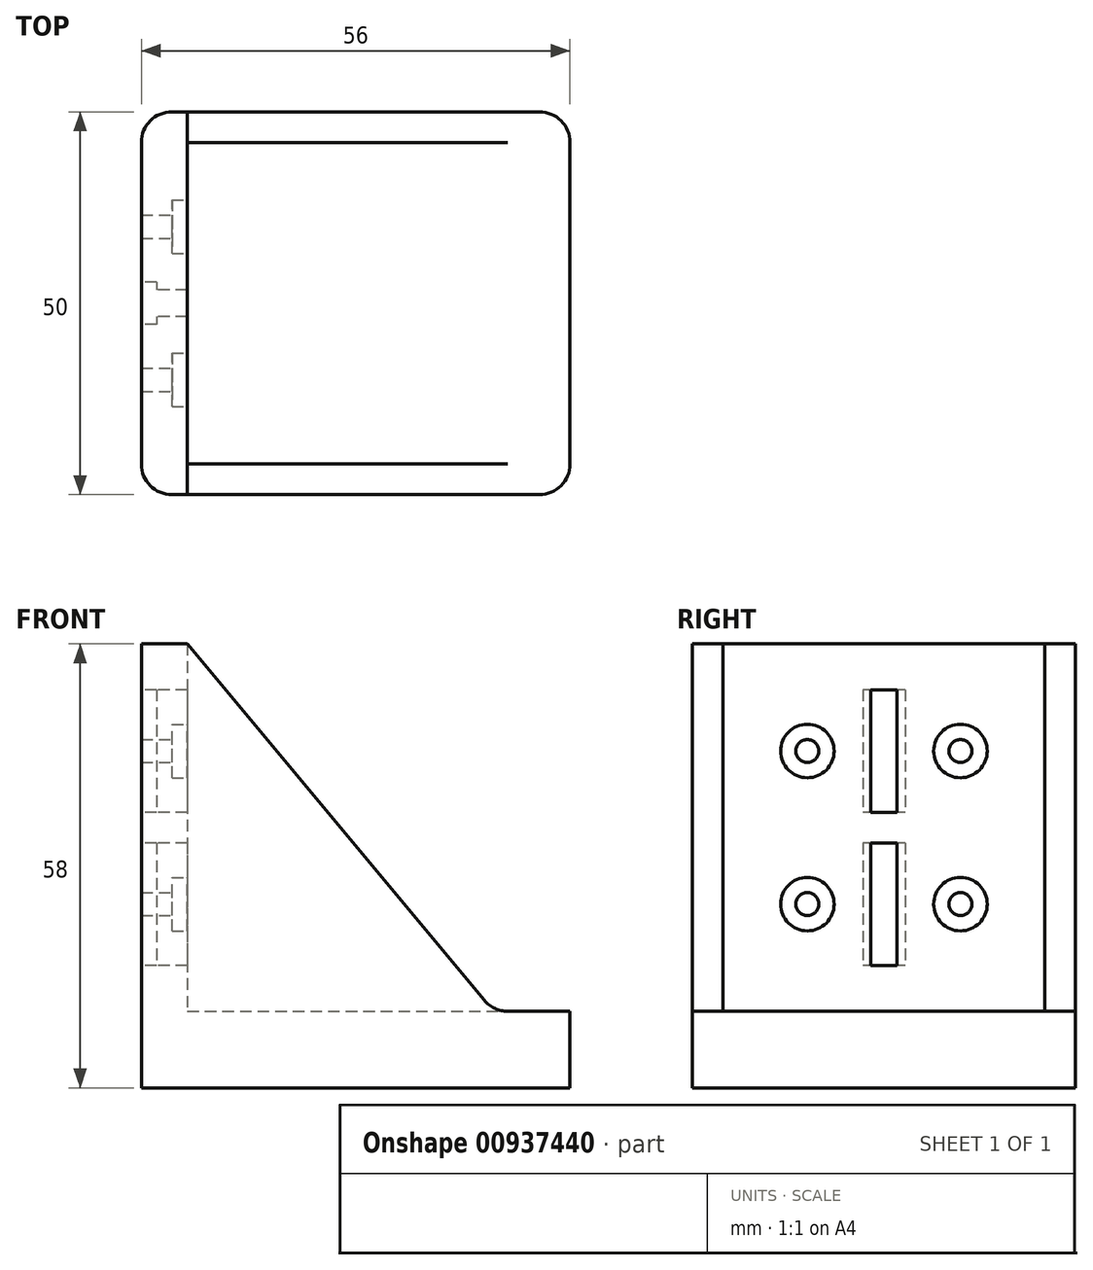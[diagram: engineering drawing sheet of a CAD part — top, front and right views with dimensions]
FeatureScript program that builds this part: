
annotation { "Feature Type Name" : "Feature", "Feature Type Description" : "" }
export const myFeature = defineFeature(function(context is Context, id is Id, definition is map)
    precondition{}
    {
        {
            var Q0;
            Q0=qCreatedBy(makeId("Top.planeOp"),FACE);
            var sketch = newSketch(context, id + "F0", { "sketchPlane" : qUnion([Q0])});
            skLineSegment(sketch, "E0.bottom", {"start": v(0, 50) * mm, "end": v(56, 50) * mm});
            skLineSegment(sketch, "E0.top", {"start": v(0, 0) * mm, "end": v(56, 0) * mm});
            skLineSegment(sketch, "E0.left", {"start": v(0, 50) * mm, "end": v(0, 0) * mm});
            skLineSegment(sketch, "E0.right", {"start": v(56, 50) * mm, "end": v(56, 0) * mm});
            skSolve(sketch);
        }
        {
            var Q0;
            Q0=qSketchRegion(id+"F0",true);
            extrude(context, id + "F1", {"entities" : qUnion([Q0]), "depth" : 10 * mm, "offsetDistance" : 25 * mm});
        }
        {
            var Q0;
            Q0=makeQuery(id+"F1.opExtrude","CAP_FACE",FACE,{"disambiguationData":[OSD([sQuery(id+"F0.wireOp",EDGE,"JcqLtr4a-4iO0-7SYc-JrXt-3wWf4lI9VCyy"),sQuery(id+"F0.wireOp",EDGE,"3zeIyssa-BI9L-WOF6-APSg-kyZtDzQDufFM"),sQuery(id+"F0.wireOp",EDGE,"Hb38dC7V-6ZDo-NrQG-Z8Se-XjxkW8JbUmMz"),sQuery(id+"F0.wireOp",EDGE,"y3aIqdCw-jFc2-MhhD-7X5v-KuRHTVy27k4Q"),sQuery(id+"F0.wireOp",EDGE,"XVNT8TL3-6rPS-E8CT-cUIb-nR5d3DAh4WGq"),sQuery(id+"F0.wireOp",EDGE,"E0.bottom"),sQuery(id+"F0.wireOp",EDGE,"E0.top"),sQuery(id+"F0.wireOp",EDGE,"E0.left"),sQuery(id+"F0.wireOp",EDGE,"E0.right")])],"isStart":false});
            var sketch = newSketch(context, id + "F2", { "sketchPlane" : qUnion([Q0])});
            skLineSegment(sketch, "E1.bottom", {"start": v(0, 50) * mm, "end": v(6, 50) * mm});
            skLineSegment(sketch, "E1.top", {"start": v(0, 0) * mm, "end": v(6, 0) * mm});
            skLineSegment(sketch, "E1.left", {"start": v(0, 50) * mm, "end": v(0, 0) * mm});
            skLineSegment(sketch, "E1.right", {"start": v(6, 50) * mm, "end": v(6, 0) * mm});
            skLineSegment(sketch, "E2.bottom", {"start": v(6, 50) * mm, "end": v(46, 50) * mm});
            skLineSegment(sketch, "E2.top", {"start": v(6, 46) * mm, "end": v(46, 46) * mm});
            skLineSegment(sketch, "E2.left", {"start": v(6, 50) * mm, "end": v(6, 46) * mm});
            skLineSegment(sketch, "E2.right", {"start": v(46, 50) * mm, "end": v(46, 46) * mm});
            skLineSegment(sketch, "E3.bottom", {"start": v(6, 0) * mm, "end": v(46, 0) * mm});
            skLineSegment(sketch, "E3.top", {"start": v(6, 4) * mm, "end": v(46, 4) * mm});
            skLineSegment(sketch, "E3.left", {"start": v(6, 0) * mm, "end": v(6, 4) * mm});
            skLineSegment(sketch, "E3.right", {"start": v(46, 0) * mm, "end": v(46, 4) * mm});
            skSolve(sketch);
        }
        {
            var Q0;
            Q0=qSketchRegion(id+"F2",true);
            extrude(context, id + "F3", {"entities" : qUnion([Q0]), "operationType" : NewBodyOperationType.ADD, "depth" : (25 + 15 + 8) * mm, "offsetDistance" : 25 * mm});
        }
        {
            var Q0;
            Q0=makeQuery(id+"F3.boolean.opBoolean","MERGE",FACE,{"derivedFrom":[makeQuery(id+"F1.opExtrude","SWEPT_FACE",FACE,{"disambiguationData":[OSD([sQuery(id+"F0.wireOp",EDGE,"E0.top")])]}),makeQuery(id+"F3.opExtrude","SWEPT_FACE",FACE,{"disambiguationData":[OSD([sQuery(id+"F2.wireOp",EDGE,"E1.top"),sQuery(id+"F2.wireOp",EDGE,"E3.bottom")])]})]});
            var sketch = newSketch(context, id + "F4", { "sketchPlane" : qUnion([Q0])});
            skLineSegment(sketch, "E4", {"start": v(46, 10) * mm, "end": v(6, 58) * mm});
            skLineSegment(sketch, "E5", {"start": v(6, 58) * mm, "end": v(46, 58) * mm});
            skLineSegment(sketch, "E6", {"start": v(46, 58) * mm, "end": v(46, 10) * mm});
            skSolve(sketch);
        }
        {
            var Q0;
            Q0 = qSketchRegion(id + "F4", true);
            extrude(context, id + "F5", {"entities" : qUnion([Q0]), "operationType" : NewBodyOperationType.REMOVE, "endBound" : BoundingType.THROUGH_ALL, "oppositeDirection" : true, "depth" : 25 * mm, "offsetDistance" : 25 * mm});
        }
        {
            var Q0;
            Q0=makeQuery(id+"F3.boolean.opBoolean","MERGE",EDGE,{"derivedFrom":[makeQuery(id+"F1.opExtrude","SWEPT_EDGE",EDGE,{"disambiguationData":[OSD([sQuery(id+"F0.wireOp",EDGE,"E0.top"),sQuery(id+"F0.wireOp",EDGE,"E0.left")])]}),makeQuery(id+"F3.opExtrude","SWEPT_EDGE",EDGE,{"disambiguationData":[OSD([sQuery(id+"F2.wireOp",EDGE,"E1.top"),sQuery(id+"F2.wireOp",EDGE,"E1.left")])]})]});
            var Q1;
            Q1=makeQuery(id+"F1.opExtrude","SWEPT_EDGE",EDGE,{"disambiguationData":[OSD([sQuery(id+"F0.wireOp",EDGE,"E0.top"),sQuery(id+"F0.wireOp",EDGE,"E0.right")])]});
            var Q2;
            Q2=makeQuery(id+"F5.boolean.opBoolean","MERGE",EDGE,{"derivedFrom":[makeQuery(id+"F3.opExtrude","CAP_EDGE",EDGE,{"disambiguationData":[OSD([sQuery(id+"F2.wireOp",EDGE,"E3.right")])],"isStart":true})],"fromTools":[makeQuery(id+"F5.opExtrude","SWEPT_EDGE",EDGE,{"disambiguationData":[OSD([sQuery(id+"F0.wireOp",EDGE,"E0.top"),sQuery(id+"F4.wireOp",EDGE,"E4"),sQuery(id+"F4.wireOp",EDGE,"E6")])]})]});
            var Q3;
            Q3=makeQuery(id+"F5.boolean.opBoolean","MERGE",EDGE,{"derivedFrom":[makeQuery(id+"F3.opExtrude","CAP_EDGE",EDGE,{"disambiguationData":[OSD([sQuery(id+"F2.wireOp",EDGE,"E2.right")])],"isStart":true})],"fromTools":[makeQuery(id+"F5.opExtrude","SWEPT_EDGE",EDGE,{"disambiguationData":[OSD([sQuery(id+"F0.wireOp",EDGE,"E0.top"),sQuery(id+"F4.wireOp",EDGE,"E4"),sQuery(id+"F4.wireOp",EDGE,"E6")])]})]});
            var Q4;
            Q4=makeQuery(id+"F1.opExtrude","SWEPT_EDGE",EDGE,{"disambiguationData":[OSD([sQuery(id+"F0.wireOp",EDGE,"E0.bottom"),sQuery(id+"F0.wireOp",EDGE,"E0.right")])]});
            var Q5;
            Q5=makeQuery(id+"F3.boolean.opBoolean","MERGE",EDGE,{"derivedFrom":[makeQuery(id+"F1.opExtrude","SWEPT_EDGE",EDGE,{"disambiguationData":[OSD([sQuery(id+"F0.wireOp",EDGE,"E0.bottom"),sQuery(id+"F0.wireOp",EDGE,"E0.left")])]}),makeQuery(id+"F3.opExtrude","SWEPT_EDGE",EDGE,{"disambiguationData":[OSD([sQuery(id+"F2.wireOp",EDGE,"E1.bottom"),sQuery(id+"F2.wireOp",EDGE,"E1.left")])]})]});
            fillet(context, id + "F6", {"entities" : qUnion([Q0, Q1, Q2, Q3, Q4, Q5]), "radius" : 4 * mm, "tangentPropagation" : true, "allowEdgeOverflow" : false});
        }
        {
            var Q0;
            Q0=makeQuery(id+"F3.boolean.opBoolean","MERGE",FACE,{"derivedFrom":[makeQuery(id+"F1.opExtrude","SWEPT_FACE",FACE,{"disambiguationData":[OSD([sQuery(id+"F0.wireOp",EDGE,"E0.left")])]}),makeQuery(id+"F3.opExtrude","SWEPT_FACE",FACE,{"disambiguationData":[OSD([sQuery(id+"F2.wireOp",EDGE,"E1.left")])]})]});
            var sketch = newSketch(context, id + "F7", { "sketchPlane" : qUnion([Q0])});
            skLineSegment(sketch, "E7", {"start": v(-25, 52) * mm, "end": v(-25, 16) * mm, "construction": true});
            skLineSegment(sketch, "E8", {"start": v(-26.73, 52) * mm, "end": v(-26.73, 16) * mm});
            skLineSegment(sketch, "E9", {"start": v(-23.28, 52) * mm, "end": v(-23.28, 16) * mm});
            skLineSegment(sketch, "E10.bottom", {"start": v(-27.76, 36) * mm, "end": v(-22.24, 36) * mm});
            skLineSegment(sketch, "E10.top", {"start": v(-27.76, 32) * mm, "end": v(-22.24, 32) * mm});
            skLineSegment(sketch, "E10.left", {"start": v(-27.76, 36) * mm, "end": v(-27.76, 32) * mm});
            skLineSegment(sketch, "E10.right", {"start": v(-22.24, 36) * mm, "end": v(-22.24, 32) * mm});
            skLineSegment(sketch, "E11", {"start": v(-25, 34) * mm, "end": v(-27.76, 34) * mm, "construction": true});
            skLineSegment(sketch, "E12", {"start": v(-23.28, 52) * mm, "end": v(-26.73, 52) * mm});
            skLineSegment(sketch, "E13", {"start": v(-23.28, 16) * mm, "end": v(-26.73, 16) * mm});
            skLineSegment(sketch, "E14.bottom", {"start": v(-27.76, 52) * mm, "end": v(-22.24, 52) * mm});
            skLineSegment(sketch, "E14.top", {"start": v(-27.76, 16) * mm, "end": v(-22.24, 16) * mm});
            skLineSegment(sketch, "E14.left", {"start": v(-27.76, 52) * mm, "end": v(-27.76, 16) * mm});
            skLineSegment(sketch, "E14.right", {"start": v(-22.24, 52) * mm, "end": v(-22.24, 16) * mm});
            skLineSegment(sketch, "E15", {"start": v(-27.76, 34) * mm, "end": v(-27.76, 34) * mm});
            skLineSegment(sketch, "E16", {"start": v(-25, 58) * mm, "end": v(-25, 52) * mm, "construction": true});
            skSolve(sketch);
        }
        {
            var Q0;
            {var subQ0=sQuery(id+"F7.wireOp",EDGE,"E14.bottom");var subQ1=sQuery(id+"F7.wireOp",EDGE,"E8");var subQ2=makeQuery(id+"F7.imprint","INTERSECT",VERTEX,{"derivedFrom":[subQ1,subQ0]});Q0=makeQuery(id+"F7.imprint","IMPRINT",FACE,{"disambiguationData":[TD([[makeQuery(id+"F7.imprint","IMPRINT",EDGE,{"disambiguationData":[TD([[subQ2,-1.0]])],"derivedFrom":subQ1}),-1.0]])]});}
            var Q1;
            {var subQ0=sQuery(id+"F7.wireOp",EDGE,"E14.bottom");var subQ1=sQuery(id+"F7.wireOp",EDGE,"E9");var subQ2=makeQuery(id+"F7.imprint","INTERSECT",VERTEX,{"derivedFrom":[subQ1,subQ0]});Q1=makeQuery(id+"F7.imprint","IMPRINT",FACE,{"disambiguationData":[TD([[makeQuery(id+"F7.imprint","IMPRINT",EDGE,{"disambiguationData":[TD([[subQ2,-1.0]])],"derivedFrom":subQ1}),1.0]])]});}
            var Q2;
            {var subQ0=sQuery(id+"F7.wireOp",EDGE,"E14.top");var subQ1=sQuery(id+"F7.wireOp",EDGE,"E9");var subQ2=makeQuery(id+"F7.imprint","INTERSECT",VERTEX,{"derivedFrom":[subQ1,subQ0]});Q2=makeQuery(id+"F7.imprint","IMPRINT",FACE,{"disambiguationData":[TD([[makeQuery(id+"F7.imprint","IMPRINT",EDGE,{"disambiguationData":[TD([[subQ2,1.0]])],"derivedFrom":subQ1}),1.0]])]});}
            var Q3;
            {var subQ0=sQuery(id+"F7.wireOp",EDGE,"E14.top");var subQ1=sQuery(id+"F7.wireOp",EDGE,"E8");var subQ2=makeQuery(id+"F7.imprint","INTERSECT",VERTEX,{"derivedFrom":[subQ1,subQ0]});Q3=makeQuery(id+"F7.imprint","IMPRINT",FACE,{"disambiguationData":[TD([[makeQuery(id+"F7.imprint","IMPRINT",EDGE,{"disambiguationData":[TD([[subQ2,1.0]])],"derivedFrom":subQ1}),-1.0]])]});}
            extrude(context, id + "F8", {"entities" : qUnion([Q0, Q1, Q2, Q3]), "operationType" : NewBodyOperationType.REMOVE, "oppositeDirection" : true, "depth" : 2 * mm, "offsetDistance" : 25 * mm});
        }
        {
            var Q0;
            {var subQ0=sQuery(id+"F7.wireOp",EDGE,"E14.bottom");var subQ1=sQuery(id+"F7.wireOp",EDGE,"E8");var subQ2=makeQuery(id+"F7.imprint","INTERSECT",VERTEX,{"derivedFrom":[subQ1,subQ0]});Q0=makeQuery(id+"F7.imprint","IMPRINT",FACE,{"disambiguationData":[TD([[makeQuery(id+"F7.imprint","IMPRINT",EDGE,{"disambiguationData":[TD([[subQ2,-1.0]])],"derivedFrom":subQ1}),1.0]])]});}
            var Q1;
            {var subQ0=sQuery(id+"F7.wireOp",EDGE,"E14.top");var subQ1=sQuery(id+"F7.wireOp",EDGE,"E8");var subQ2=makeQuery(id+"F7.imprint","INTERSECT",VERTEX,{"derivedFrom":[subQ1,subQ0]});Q1=makeQuery(id+"F7.imprint","IMPRINT",FACE,{"disambiguationData":[TD([[makeQuery(id+"F7.imprint","IMPRINT",EDGE,{"disambiguationData":[TD([[subQ2,1.0]])],"derivedFrom":subQ1}),1.0]])]});}
            extrude(context, id + "F9", {"entities" : qUnion([Q0, Q1]), "operationType" : NewBodyOperationType.REMOVE, "endBound" : BoundingType.UP_TO_NEXT, "oppositeDirection" : true, "depth" : 25 * mm, "offsetDistance" : 25 * mm});
        }
        {
            var Q0;
            Q0=makeQuery(id+"F3.opExtrude","SWEPT_FACE",FACE,{"disambiguationData":[OSD([sQuery(id+"F2.wireOp",EDGE,"E1.right")])]});
            var sketch = newSketch(context, id + "F10", { "sketchPlane" : qUnion([Q0])});
            skLineSegment(sketch, "E17.bottom", {"start": v(15, 44) * mm, "end": v(35, 44) * mm, "construction": true});
            skLineSegment(sketch, "E17.top", {"start": v(15, 24) * mm, "end": v(35, 24) * mm, "construction": true});
            skLineSegment(sketch, "E17.left", {"start": v(15, 44) * mm, "end": v(15, 24) * mm, "construction": true});
            skLineSegment(sketch, "E17.right", {"start": v(35, 44) * mm, "end": v(35, 24) * mm, "construction": true});
            skCircle(sketch, "E18", {"center": v(15, 44) * mm, "radius": 1.5 * mm});
            skCircle(sketch, "E19", {"center": v(35, 44) * mm, "radius": 1.5 * mm});
            skCircle(sketch, "E20", {"center": v(35, 24) * mm, "radius": 1.5 * mm});
            skCircle(sketch, "E21", {"center": v(15, 24) * mm, "radius": 1.5 * mm});
            skCircle(sketch, "E22", {"center": v(15, 44) * mm, "radius": 3.5 * mm});
            skCircle(sketch, "E23", {"center": v(35, 44) * mm, "radius": 3.5 * mm});
            skCircle(sketch, "E24", {"center": v(35, 24) * mm, "radius": 3.5 * mm});
            skCircle(sketch, "E25", {"center": v(15, 24) * mm, "radius": 3.5 * mm});
            skLineSegment(sketch, "E26", {"start": v(25, 58) * mm, "end": v(25, 44) * mm, "construction": true});
            skSolve(sketch);
        }
        {
            var Q0;
            Q0=qSketchRegion(id+"F10",true);
            extrude(context, id + "F11", {"entities" : qUnion([Q0]), "operationType" : NewBodyOperationType.REMOVE, "oppositeDirection" : true, "depth" : 2 * mm, "offsetDistance" : 25 * mm});
        }
        {
            var Q0;
            Q0=makeQuery(id+"F10.imprint","IMPRINT",FACE,{"disambiguationData":[TD([[makeQuery(id+"F10.imprint","IMPRINT",EDGE,{"derivedFrom":sQuery(id+"F10.wireOp",EDGE,"E18")}),1.0]])]});
            var Q1;
            Q1=makeQuery(id+"F10.imprint","IMPRINT",FACE,{"disambiguationData":[TD([[makeQuery(id+"F10.imprint","IMPRINT",EDGE,{"derivedFrom":sQuery(id+"F10.wireOp",EDGE,"E19")}),1.0]])]});
            var Q2;
            Q2=makeQuery(id+"F10.imprint","IMPRINT",FACE,{"disambiguationData":[TD([[makeQuery(id+"F10.imprint","IMPRINT",EDGE,{"derivedFrom":sQuery(id+"F10.wireOp",EDGE,"E20")}),1.0]])]});
            var Q3;
            Q3=makeQuery(id+"F10.imprint","IMPRINT",FACE,{"disambiguationData":[TD([[makeQuery(id+"F10.imprint","IMPRINT",EDGE,{"derivedFrom":sQuery(id+"F10.wireOp",EDGE,"E21")}),1.0]])]});
            extrude(context, id + "F12", {"entities" : qUnion([Q0, Q1, Q2, Q3]), "operationType" : NewBodyOperationType.REMOVE, "endBound" : BoundingType.UP_TO_NEXT, "oppositeDirection" : true, "depth" : 25 * mm, "offsetDistance" : 25 * mm});
        }
    });
